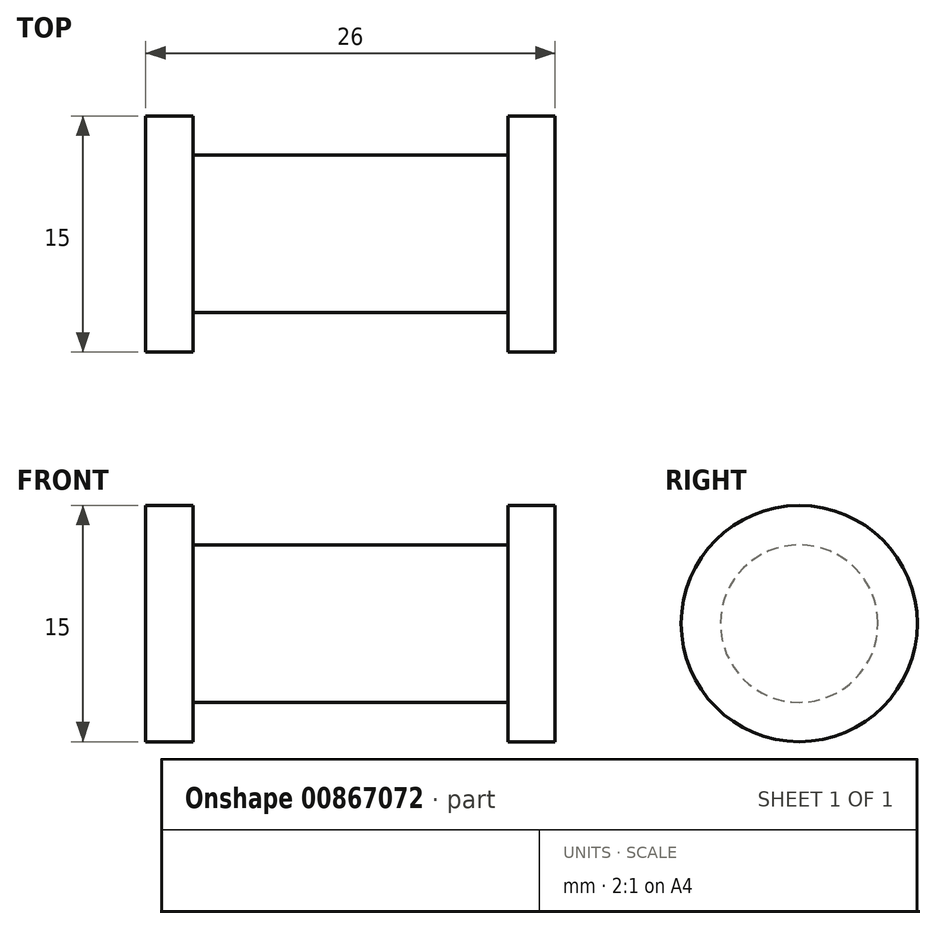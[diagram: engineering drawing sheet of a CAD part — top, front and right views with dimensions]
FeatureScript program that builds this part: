
annotation { "Feature Type Name" : "Feature", "Feature Type Description" : "" }
export const myFeature = defineFeature(function(context is Context, id is Id, definition is map)
    precondition{}
    {
        {
            var Q0;
            Q0=qCreatedBy(makeId("Top.planeOp"),FACE);
            var sketch = newSketch(context, id + "F0", { "sketchPlane" : qUnion([Q0])});
            skLineSegment(sketch, "E0.bottom", {"start": v(-10, 5) * mm, "end": v(10, 5) * mm});
            skLineSegment(sketch, "E0.top", {"start": v(-10, -5) * mm, "end": v(10, -5) * mm});
            skLineSegment(sketch, "E0.left", {"start": v(-10, 5) * mm, "end": v(-10, -5) * mm});
            skLineSegment(sketch, "E0.right", {"start": v(10, 5) * mm, "end": v(10, -5) * mm});
            skPoint(sketch, "E0.middle", {"position": v(0, 0) * mm});
            skPoint(sketch, "E1.middle", {"position": v(-10, 0) * mm});
            skLineSegment(sketch, "E2", {"start": v(-6.8, -5) * mm, "end": v(-10, -5) * mm});
            skPoint(sketch, "E3", {"position": v(10, 0) * mm});
            skLineSegment(sketch, "E4.bottom", {"start": v(-10, 7.5) * mm, "end": v(-13, 7.5) * mm});
            skLineSegment(sketch, "E4.top", {"start": v(-10, -7.5) * mm, "end": v(-13, -7.5) * mm});
            skLineSegment(sketch, "E4.left", {"start": v(-10, -7.5) * mm, "end": v(-10, 7.5) * mm});
            skLineSegment(sketch, "E4.right", {"start": v(-13, -7.5) * mm, "end": v(-13, 7.5) * mm});
            skPoint(sketch, "E4.middle", {"position": v(-11.5, 0) * mm});
            skLineSegment(sketch, "E5.bottom", {"start": v(13, -7.5) * mm, "end": v(10, -7.5) * mm});
            skLineSegment(sketch, "E5.top", {"start": v(13, 7.5) * mm, "end": v(10, 7.5) * mm});
            skLineSegment(sketch, "E5.left", {"start": v(13, -7.5) * mm, "end": v(13, 7.5) * mm});
            skLineSegment(sketch, "E5.right", {"start": v(10, -7.5) * mm, "end": v(10, 7.5) * mm});
            skPoint(sketch, "E5.middle", {"position": v(11.5, 0) * mm});
            skLineSegment(sketch, "E6", {"start": v(-13, 0) * mm, "end": v(13, 0) * mm});
            skSolve(sketch);
        }
        {
            var Q0;
            {var subQ1=sQuery(id+"F0.wireOp",EDGE,"E4.bottom");Q0=makeQuery(id+"F0.imprint","IMPRINT",FACE,{"disambiguationData":[TD([[makeQuery(id+"F0.imprint","IMPRINT",EDGE,{"derivedFrom":subQ1}),1.0]])]});}
            var Q1;
            {var subQ0=sQuery(id+"F0.wireOp",EDGE,"E0.bottom");Q1=makeQuery(id+"F0.imprint","IMPRINT",FACE,{"disambiguationData":[TD([[makeQuery(id+"F0.imprint","IMPRINT",EDGE,{"derivedFrom":subQ0}),-1.0]])]});}
            var Q2;
            {var subQ2=sQuery(id+"F0.wireOp",EDGE,"E5.top");Q2=makeQuery(id+"F0.imprint","IMPRINT",FACE,{"disambiguationData":[TD([[makeQuery(id+"F0.imprint","IMPRINT",EDGE,{"derivedFrom":subQ2}),1.0]])]});}
            var Q3;
            Q3=sQuery(id+"F0.wireOp",EDGE,"E6");
            revolve(context, id + "F1", {"surfaceOperationType" : NewSurfaceOperationType.NEW, "entities" : qUnion([Q0, Q1, Q2]), "axis" : qUnion([Q3]), "revolveType" : RevolveType.FULL});
        }
    });
